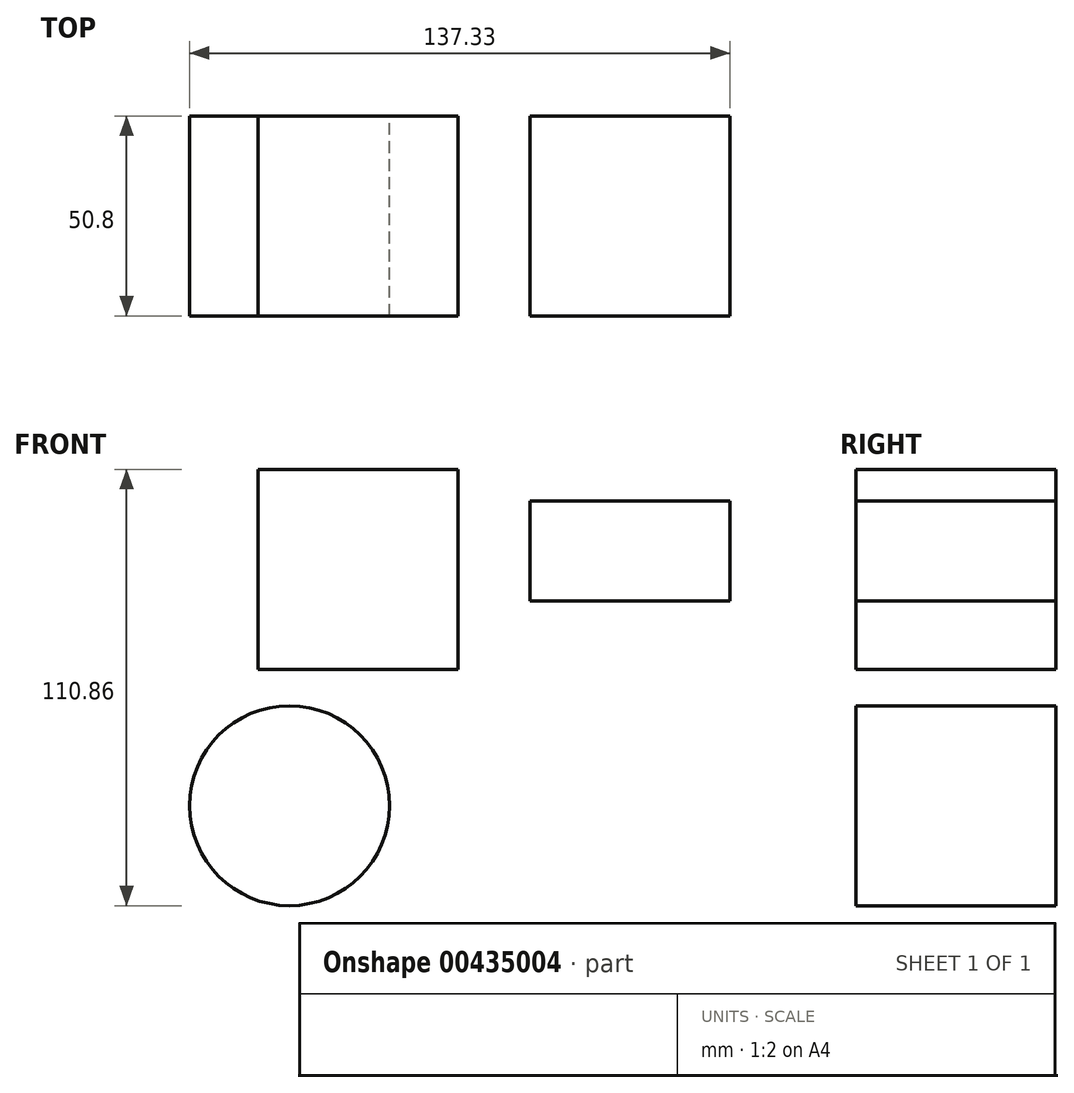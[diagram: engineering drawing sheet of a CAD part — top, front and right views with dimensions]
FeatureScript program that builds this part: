
annotation { "Feature Type Name" : "Feature", "Feature Type Description" : "" }
export const myFeature = defineFeature(function(context is Context, id is Id, definition is map)
    precondition{}
    {
        {
            var Q0;
            Q0=qCreatedBy(makeId("Front.planeOp"),FACE);
            var sketch = newSketch(context, id + "F0", { "sketchPlane" : qUnion([Q0])});
            skLineSegment(sketch, "E0.bottom", {"start": v(-57.03, 62.67) * mm, "end": v(-6.23, 62.67) * mm});
            skLineSegment(sketch, "E0.top", {"start": v(-57.03, 11.87) * mm, "end": v(-6.23, 11.87) * mm});
            skLineSegment(sketch, "E0.left", {"start": v(-57.03, 62.67) * mm, "end": v(-57.03, 11.87) * mm});
            skLineSegment(sketch, "E0.right", {"start": v(-6.23, 62.67) * mm, "end": v(-6.23, 11.87) * mm});
            skSolve(sketch);
        }
        {
            var Q0;
            Q0=qCreatedBy(makeId("Front.planeOp"),FACE);
            var sketch = newSketch(context, id + "F1", { "sketchPlane" : qUnion([Q0])});
            skLineSegment(sketch, "E1.bottom", {"start": v(12.05, 54.64) * mm, "end": v(62.85, 54.64) * mm});
            skLineSegment(sketch, "E1.top", {"start": v(12.05, 29.24) * mm, "end": v(62.85, 29.24) * mm});
            skLineSegment(sketch, "E1.left", {"start": v(12.05, 54.64) * mm, "end": v(12.05, 29.24) * mm});
            skLineSegment(sketch, "E1.right", {"start": v(62.85, 54.64) * mm, "end": v(62.85, 29.24) * mm});
            skSolve(sketch);
        }
        {
            var Q0;
            Q0=qCreatedBy(makeId("Front.planeOp"),FACE);
            var sketch = newSketch(context, id + "F2", { "sketchPlane" : qUnion([Q0])});
            skCircle(sketch, "E2", {"center": v(-49.08, -22.8) * mm, "radius": 25.4 * mm});
            skSolve(sketch);
        }
        {
            var Q0;
            Q0=makeQuery(id+"F0.imprint","IMPRINT",FACE,{"disambiguationData":[TD([[makeQuery(id+"F0.imprint","IMPRINT",EDGE,{"derivedFrom":sQuery(id+"F0.wireOp",EDGE,"E0.bottom")}),-1.0]])]});
            extrude(context, id + "F3", {"entities" : qUnion([Q0]), "depth" : 50.8 * mm});
        }
        {
            var Q0;
            Q0 = qSketchRegion(id + "F1", true);
            extrude(context, id + "F4", {"entities" : qUnion([Q0]), "depth" : 50.8 * mm});
        }
        {
            var Q0;
            Q0 = qSketchRegion(id + "F2", true);
            extrude(context, id + "F5", {"entities" : qUnion([Q0]), "depth" : 50.8 * mm});
        }
    });
